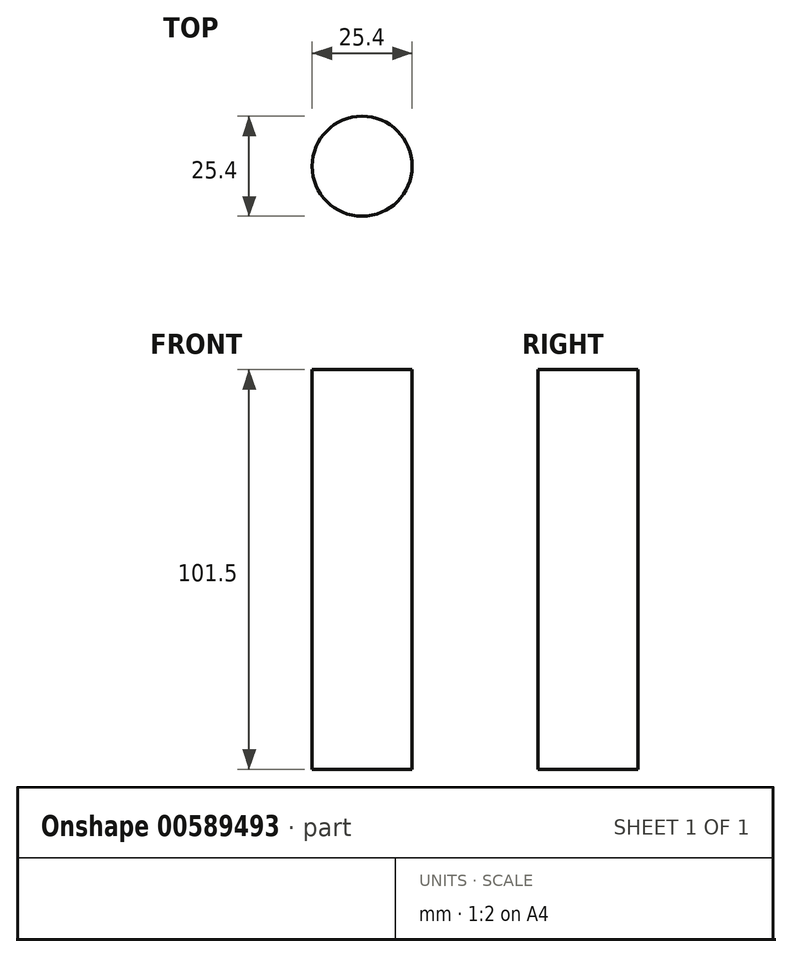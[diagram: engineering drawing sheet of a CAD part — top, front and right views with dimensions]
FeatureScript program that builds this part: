
annotation { "Feature Type Name" : "Feature", "Feature Type Description" : "" }
export const myFeature = defineFeature(function(context is Context, id is Id, definition is map)
    precondition{}
    {
        {
            var Q0;
            Q0=qCreatedBy(makeId("Top.planeOp"),FACE);
            var sketch = newSketch(context, id + "F0", { "sketchPlane" : qUnion([Q0])});
            skCircle(sketch, "E0", {"center": v(0, 0) * mm, "radius": 12.7 * mm});
            skSolve(sketch);
        }
        {
            var Q0;
            Q0=makeQuery(id+"F0.imprint","IMPRINT",FACE,{"disambiguationData":[TD([[makeQuery(id+"F0.imprint","IMPRINT",EDGE,{"derivedFrom":sQuery(id+"F0.wireOp",EDGE,"E0")}),1.0]])]});
            extrude(context, id + "F1", {"entities" : qUnion([Q0]), "depth" : 101.5 * mm, "offsetDistance" : 30.48 * mm});
        }
    });
